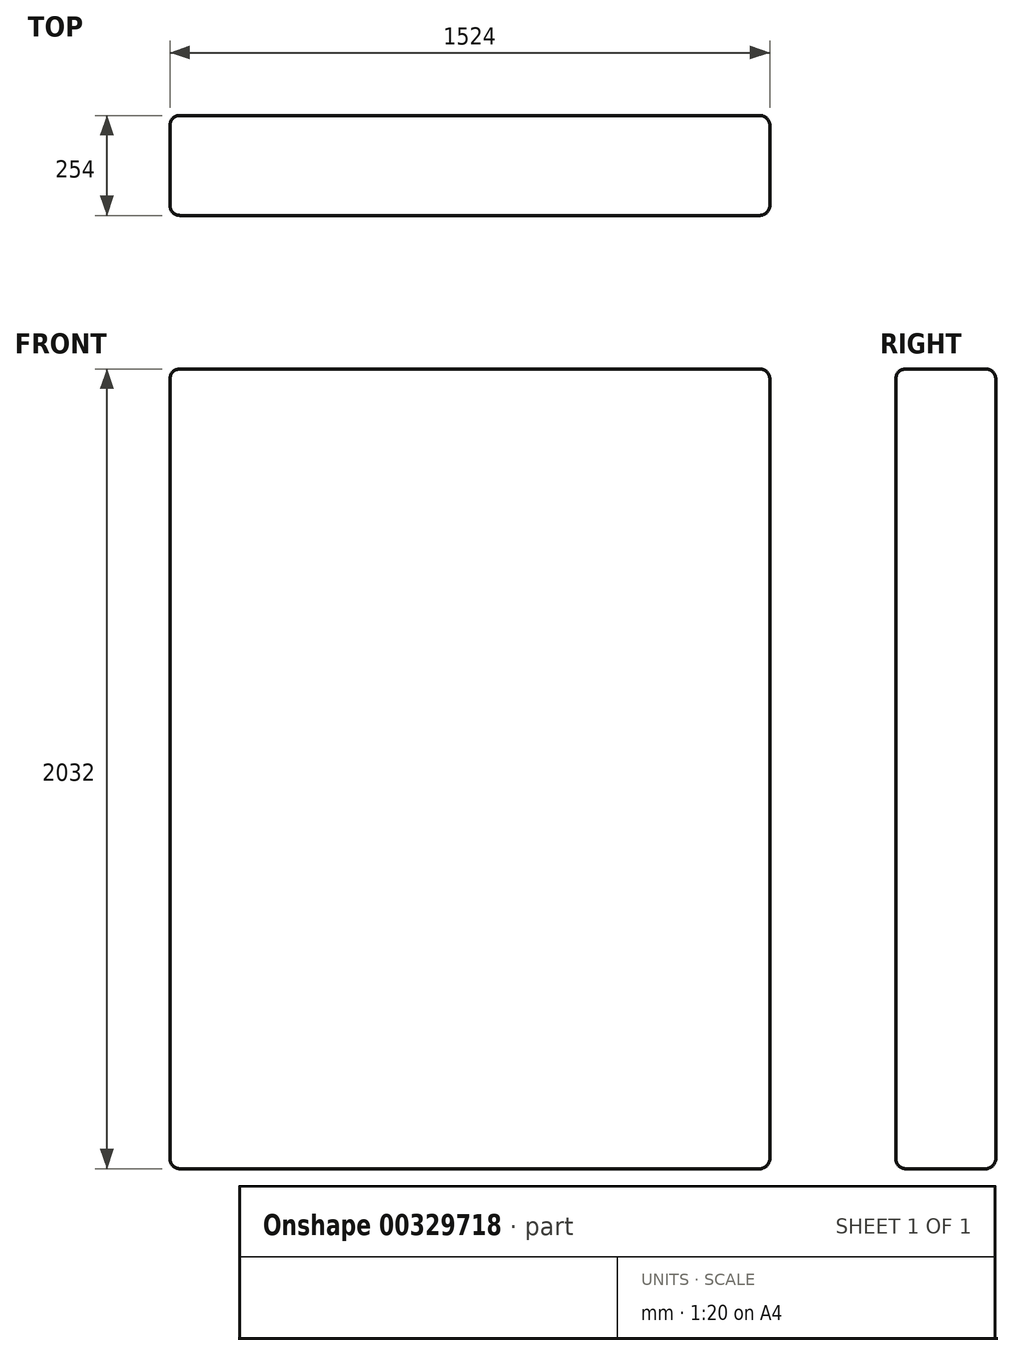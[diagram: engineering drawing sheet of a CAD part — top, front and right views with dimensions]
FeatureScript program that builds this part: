
annotation { "Feature Type Name" : "Feature", "Feature Type Description" : "" }
export const myFeature = defineFeature(function(context is Context, id is Id, definition is map)
    precondition{}
    {
        {
            var Q0;
            Q0=qCreatedBy(makeId("Front.planeOp"),FACE);
            var sketch = newSketch(context, id + "F0", { "sketchPlane" : qUnion([Q0])});
            skLineSegment(sketch, "E0.bottom", {"start": v(-762, 1016) * mm, "end": v(762, 1016) * mm});
            skLineSegment(sketch, "E0.top", {"start": v(-762, -1016) * mm, "end": v(762, -1016) * mm});
            skLineSegment(sketch, "E0.left", {"start": v(-762, 1016) * mm, "end": v(-762, -1016) * mm});
            skLineSegment(sketch, "E0.right", {"start": v(762, 1016) * mm, "end": v(762, -1016) * mm});
            skPoint(sketch, "E0.middle", {"position": v(0, 0) * mm});
            skSolve(sketch);
        }
        {
            var Q0;
            Q0=makeQuery(id+"F0.imprint","IMPRINT",FACE,{"disambiguationData":[TD([[makeQuery(id+"F0.imprint","IMPRINT",EDGE,{"derivedFrom":sQuery(id+"F0.wireOp",EDGE,"E0.bottom")}),-1.0]])]});
            extrude(context, id + "F1", {"entities" : qUnion([Q0]), "endBound" : BoundingType.SYMMETRIC, "depth" : 254 * mm});
        }
        {
            var Q0;
            Q0=makeQuery(id+"F1.opExtrude","CAP_EDGE",EDGE,{"disambiguationData":[OSD([sQuery(id+"F0.wireOp",EDGE,"E0.right")])],"isStart":false});
            var Q1;
            Q1=makeQuery(id+"F1.opExtrude","CAP_EDGE",EDGE,{"disambiguationData":[OSD([sQuery(id+"F0.wireOp",EDGE,"E0.right")])],"isStart":true});
            var Q2;
            Q2=makeQuery(id+"F1.opExtrude","SWEPT_EDGE",EDGE,{"disambiguationData":[OSD([sQuery(id+"F0.wireOp",EDGE,"E0.bottom"),sQuery(id+"F0.wireOp",EDGE,"E0.right")])]});
            var Q3;
            Q3=makeQuery(id+"F1.opExtrude","CAP_EDGE",EDGE,{"disambiguationData":[OSD([sQuery(id+"F0.wireOp",EDGE,"E0.bottom")])],"isStart":false});
            var Q4;
            Q4=makeQuery(id+"F1.opExtrude","CAP_EDGE",EDGE,{"disambiguationData":[OSD([sQuery(id+"F0.wireOp",EDGE,"E0.left")])],"isStart":false});
            var Q5;
            Q5=makeQuery(id+"F1.opExtrude","SWEPT_EDGE",EDGE,{"disambiguationData":[OSD([sQuery(id+"F0.wireOp",EDGE,"E0.bottom"),sQuery(id+"F0.wireOp",EDGE,"E0.left")])]});
            var Q6;
            Q6=makeQuery(id+"F1.opExtrude","CAP_EDGE",EDGE,{"disambiguationData":[OSD([sQuery(id+"F0.wireOp",EDGE,"E0.bottom")])],"isStart":true});
            var Q7;
            Q7=makeQuery(id+"F1.opExtrude","CAP_EDGE",EDGE,{"disambiguationData":[OSD([sQuery(id+"F0.wireOp",EDGE,"E0.left")])],"isStart":true});
            var Q8;
            Q8=makeQuery(id+"F1.opExtrude","CAP_EDGE",EDGE,{"disambiguationData":[OSD([sQuery(id+"F0.wireOp",EDGE,"E0.top")])],"isStart":true});
            var Q9;
            Q9=makeQuery(id+"F1.opExtrude","SWEPT_EDGE",EDGE,{"disambiguationData":[OSD([sQuery(id+"F0.wireOp",EDGE,"E0.top"),sQuery(id+"F0.wireOp",EDGE,"E0.left")])]});
            var Q10;
            Q10=makeQuery(id+"F1.opExtrude","CAP_EDGE",EDGE,{"disambiguationData":[OSD([sQuery(id+"F0.wireOp",EDGE,"E0.top")])],"isStart":false});
            var Q11;
            Q11=makeQuery(id+"F1.opExtrude","SWEPT_EDGE",EDGE,{"disambiguationData":[OSD([sQuery(id+"F0.wireOp",EDGE,"E0.top"),sQuery(id+"F0.wireOp",EDGE,"E0.right")])]});
            fillet(context, id + "F2", {"entities" : qUnion([Q0, Q1, Q2, Q3, Q4, Q5, Q6, Q7, Q8, Q9, Q10, Q11]), "radius" : 25.4 * mm, "tangentPropagation" : true, "allowEdgeOverflow" : false});
        }
    });
